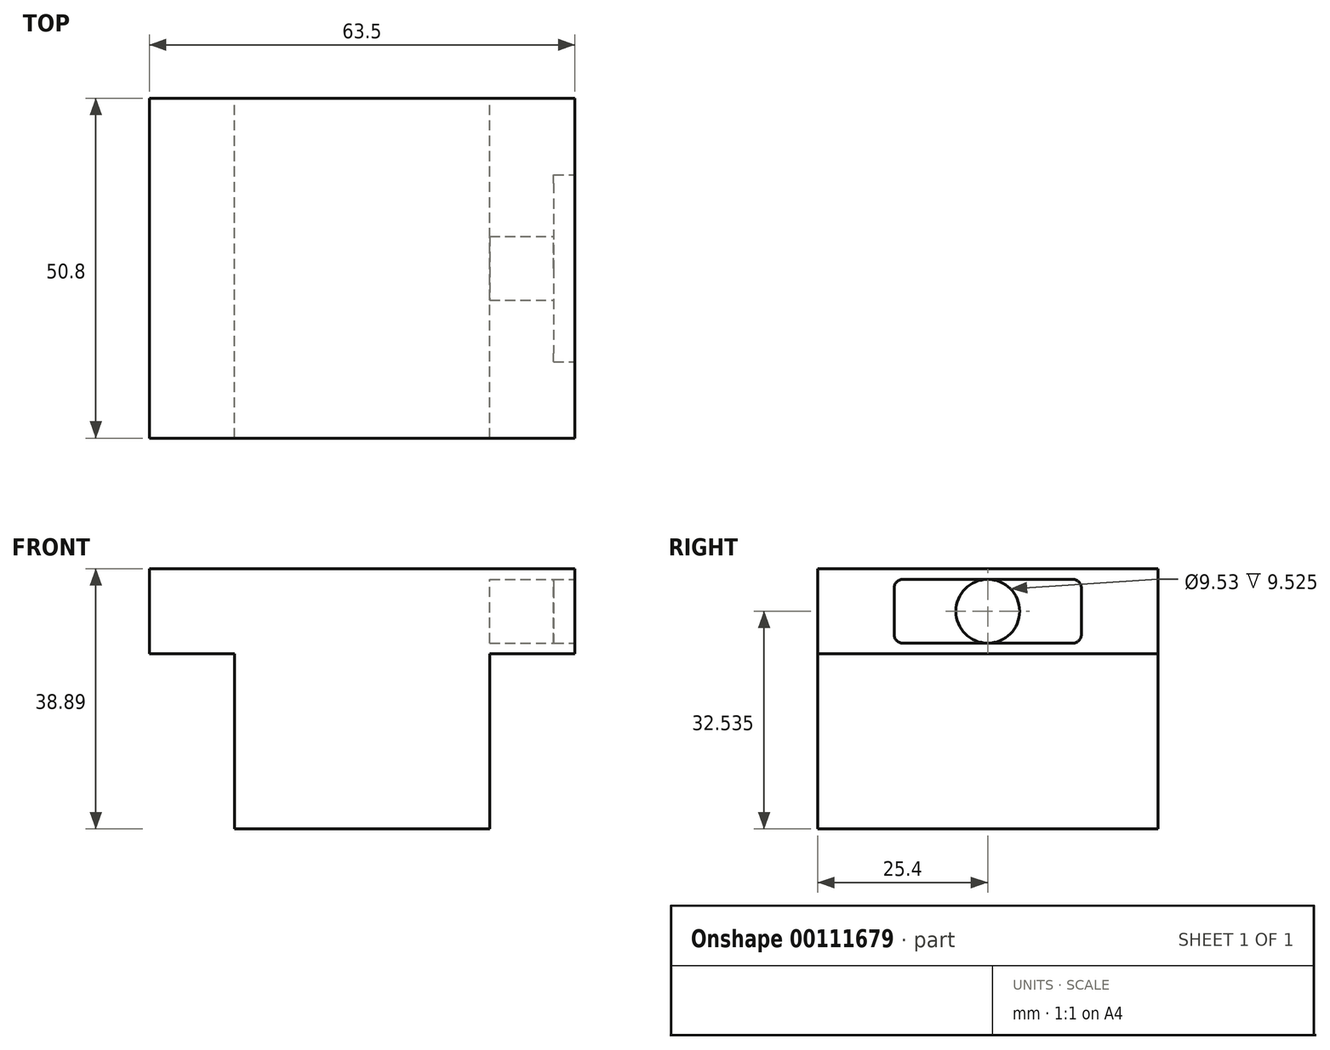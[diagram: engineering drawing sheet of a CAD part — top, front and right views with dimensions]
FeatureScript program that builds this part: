
annotation { "Feature Type Name" : "Feature", "Feature Type Description" : "" }
export const myFeature = defineFeature(function(context is Context, id is Id, definition is map)
    precondition{}
    {
        {
            var Q0;
            Q0=qCreatedBy(makeId("Front.planeOp"),FACE);
            var sketch = newSketch(context, id + "F0", { "sketchPlane" : qUnion([Q0])});
            skLineSegment(sketch, "E0.top", {"start": v(38.1, -3.18) * mm, "end": v(-25.4, -3.18) * mm});
            skPoint(sketch, "E0.middle", {"position": v(0, 0) * mm});
            skLineSegment(sketch, "E1", {"start": v(-25.4, -3.18) * mm, "end": v(-25.4, -15.88) * mm});
            skLineSegment(sketch, "E2", {"start": v(-25.4, -15.88) * mm, "end": v(-12.7, -15.88) * mm});
            skLineSegment(sketch, "E3", {"start": v(-12.7, -15.88) * mm, "end": v(-12.7, -22.23) * mm});
            skLineSegment(sketch, "E4", {"start": v(38.1, -3.18) * mm, "end": v(38.1, -15.88) * mm});
            skLineSegment(sketch, "E5", {"start": v(38.1, -15.88) * mm, "end": v(25.4, -15.88) * mm});
            skLineSegment(sketch, "E6", {"start": v(25.4, -15.88) * mm, "end": v(25.4, -22.23) * mm});
            skLineSegment(sketch, "E7", {"start": v(-12.7, -22.23) * mm, "end": v(-12.7, -42.06) * mm});
            skLineSegment(sketch, "E8", {"start": v(-12.7, -42.06) * mm, "end": v(25.4, -42.06) * mm});
            skLineSegment(sketch, "E9", {"start": v(25.4, -42.06) * mm, "end": v(25.4, -22.23) * mm});
            skSolve(sketch);
        }
        {
            var Q0;
            Q0=makeQuery(id+"F0.imprint","IMPRINT",FACE,{"disambiguationData":[TD([[makeQuery(id+"F0.imprint","IMPRINT",EDGE,{"derivedFrom":sQuery(id+"F0.wireOp",EDGE,"E0.top")}),1.0]])]});
            extrude(context, id + "F1", {"entities" : qUnion([Q0]), "depth" : 50.8 * mm});
        }
        {
            var Q0;
            Q0=makeQuery(id+"F1.opExtrude","SWEPT_FACE",FACE,{"disambiguationData":[OSD([sQuery(id+"F0.wireOp",EDGE,"E4")])]});
            var sketch = newSketch(context, id + "F2", { "sketchPlane" : qUnion([Q0])});
            skCircle(sketch, "E10", {"center": v(-25.4, -9.53) * mm, "radius": 4.76 * mm});
            skPoint(sketch, "E10.centerSnap0", {"position": v(-25.4, -3.17) * mm});
            skPoint(sketch, "E10.centerSnap1", {"position": v(-50.8, -9.53) * mm});
            skSolve(sketch);
        }
        {
            var Q0;
            Q0=makeQuery(id+"F2.imprint","IMPRINT",FACE,{"disambiguationData":[TD([[makeQuery(id+"F2.imprint","IMPRINT",EDGE,{"derivedFrom":sQuery(id+"F2.wireOp",EDGE,"E10")}),1.0]])]});
            extrude(context, id + "F3", {"entities" : qUnion([Q0]), "operationType" : NewBodyOperationType.REMOVE, "oppositeDirection" : true, "depth" : 12.7 * mm});
        }
        {
            var Q0;
            Q0=makeQuery(id+"F1.opExtrude","SWEPT_FACE",FACE,{"disambiguationData":[OSD([sQuery(id+"F0.wireOp",EDGE,"E4")])]});
            var sketch = newSketch(context, id + "F4", { "sketchPlane" : qUnion([Q0])});
            skLineSegment(sketch, "E11", {"start": v(-25.4, -14.29) * mm, "end": v(-38.1, -14.29) * mm});
            skPoint(sketch, "E11.startSnap0", {"position": v(-25.4, -3.17) * mm});
            skLineSegment(sketch, "E12", {"start": v(-25.4, -4.76) * mm, "end": v(-38.1, -4.76) * mm});
            skLineSegment(sketch, "E13", {"start": v(-25.4, -4.76) * mm, "end": v(-18.37, -4.76) * mm});
            skLineSegment(sketch, "E14", {"start": v(-11.43, -9.84) * mm, "end": v(-11.43, -13.02) * mm});
            skLineSegment(sketch, "E15", {"start": v(-12.7, -14.29) * mm, "end": v(-25.4, -14.29) * mm});
            skLineSegment(sketch, "E16", {"start": v(-39.37, -6.03) * mm, "end": v(-39.37, -13.02) * mm});
            skPoint(sketch, "E17.visualSharp", {"position": v(-11.43, -4.76) * mm});
            skPoint(sketch, "E18.visualSharp", {"position": v(-39.37, -4.76) * mm});
            skArc(sketch, "E18.filletArc", {"start": v(-38.1, -4.76) * mm, "mid": v(-39, -5.13) * mm, "end": v(-39.37, -6.03) * mm});
            skPoint(sketch, "E19.visualSharp", {"position": v(-39.37, -14.29) * mm});
            skArc(sketch, "E19.filletArc", {"start": v(-39.37, -13.02) * mm, "mid": v(-39, -13.92) * mm, "end": v(-38.1, -14.29) * mm});
            skPoint(sketch, "E20.visualSharp", {"position": v(-11.43, -14.29) * mm});
            skArc(sketch, "E20.filletArc", {"start": v(-12.7, -14.29) * mm, "mid": v(-11.8, -13.92) * mm, "end": v(-11.43, -13.02) * mm});
            skLineSegment(sketch, "E21", {"start": v(-18.37, -4.76) * mm, "end": v(-12.7, -4.76) * mm});
            skLineSegment(sketch, "E22", {"start": v(-11.43, -9.84) * mm, "end": v(-11.43, -6.03) * mm});
            skArc(sketch, "E23.filletArc", {"start": v(-11.43, -6.03) * mm, "mid": v(-11.8, -5.13) * mm, "end": v(-12.7, -4.76) * mm});
            skSolve(sketch);
        }
        {
            var Q0;
            {var subQ2=sQuery(id+"F4.wireOp",EDGE,"E13");Q0=makeQuery(id+"F4.imprint","IMPRINT",FACE,{"disambiguationData":[TD([[makeQuery(id+"F4.imprint","IMPRINT",EDGE,{"derivedFrom":subQ2}),-1.0]])]});}
            var Q1;
            {var subQ1=sQuery(id+"F4.wireOp",EDGE,"E11");Q1=makeQuery(id+"F4.imprint","IMPRINT",FACE,{"disambiguationData":[TD([[makeQuery(id+"F4.imprint","IMPRINT",EDGE,{"derivedFrom":subQ1}),-1.0]])]});}
            extrude(context, id + "F5", {"entities" : qUnion([Q0, Q1]), "operationType" : NewBodyOperationType.REMOVE, "oppositeDirection" : true, "depth" : 3.17 * mm});
        }
    });
